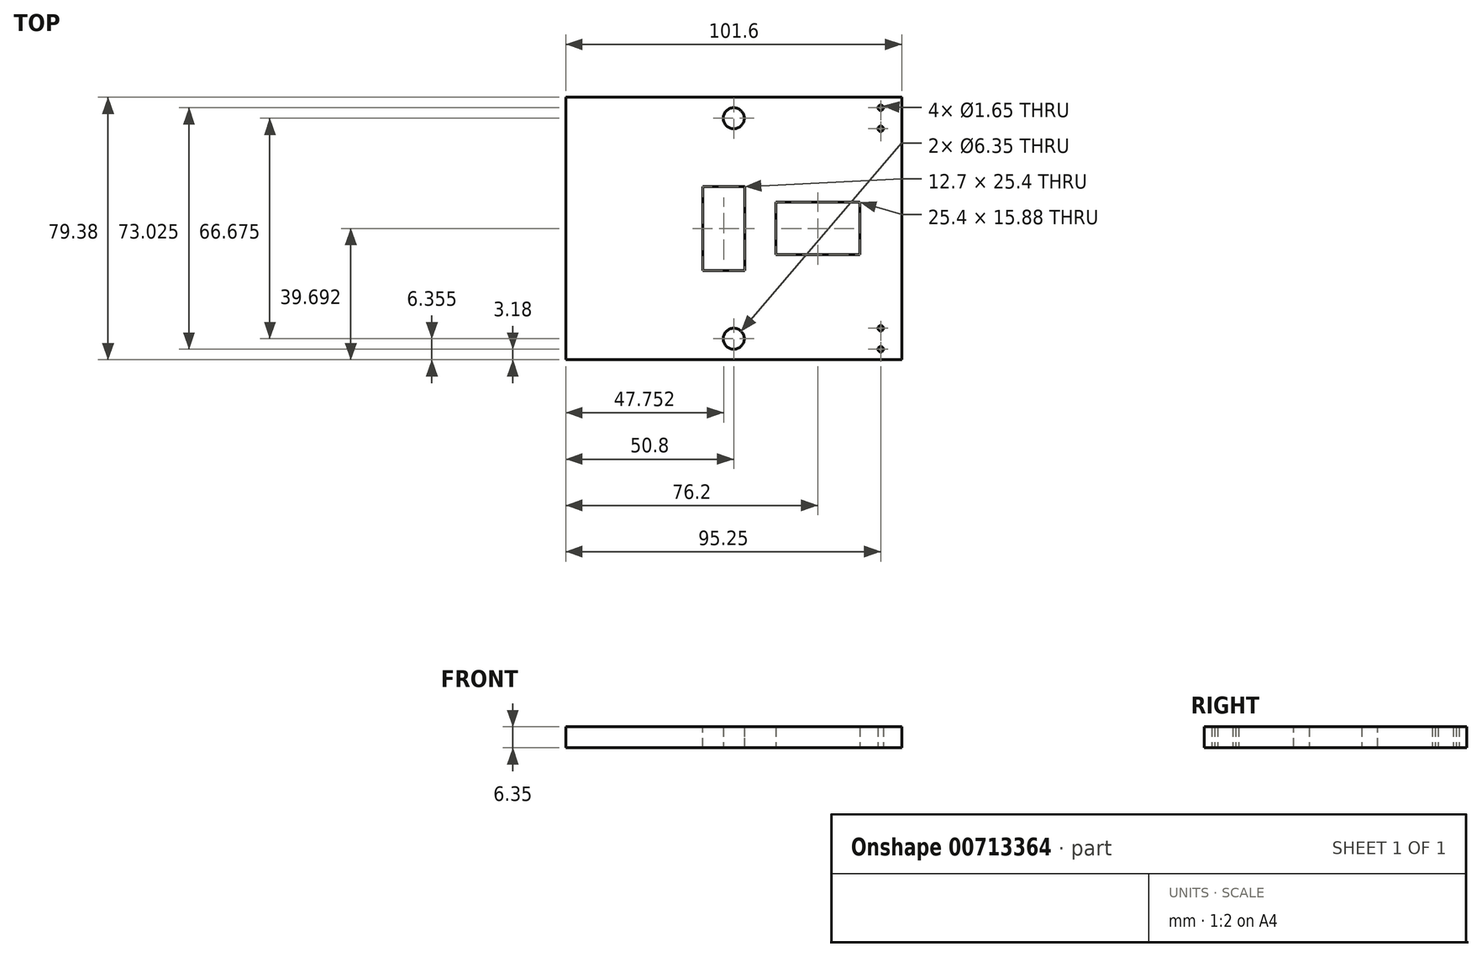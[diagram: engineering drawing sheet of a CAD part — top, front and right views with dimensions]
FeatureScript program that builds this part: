
annotation { "Feature Type Name" : "Feature", "Feature Type Description" : "" }
export const myFeature = defineFeature(function(context is Context, id is Id, definition is map)
    precondition{}
    {
        {
            var Q0;
            Q0=qCreatedBy(makeId("Top.planeOp"),FACE);
            var sketch = newSketch(context, id + "F0", { "sketchPlane" : qUnion([Q0])});
            skLineSegment(sketch, "E0.bottom", {"start": v(0, 0) * mm, "end": v(-101.6, 0) * mm});
            skLineSegment(sketch, "E0.top", {"start": v(0, -79.38) * mm, "end": v(-101.6, -79.38) * mm});
            skLineSegment(sketch, "E0.left", {"start": v(0, 0) * mm, "end": v(0, -79.38) * mm});
            skLineSegment(sketch, "E0.right", {"start": v(-101.6, 0) * mm, "end": v(-101.6, -79.38) * mm});
            skLineSegment(sketch, "E1.bottom", {"start": v(0, 0) * mm, "end": v(-12.7, 0) * mm});
            skLineSegment(sketch, "E1.top", {"start": v(0, -12.7) * mm, "end": v(-12.7, -12.7) * mm});
            skLineSegment(sketch, "E1.left", {"start": v(0, 0) * mm, "end": v(0, -12.7) * mm});
            skLineSegment(sketch, "E1.right", {"start": v(-12.7, 0) * mm, "end": v(-12.7, -12.7) * mm});
            skLineSegment(sketch, "E2.bottom", {"start": v(0, -79.38) * mm, "end": v(-12.7, -79.38) * mm});
            skLineSegment(sketch, "E2.top", {"start": v(0, -66.67) * mm, "end": v(-12.7, -66.67) * mm});
            skLineSegment(sketch, "E2.left", {"start": v(0, -79.38) * mm, "end": v(0, -66.67) * mm});
            skLineSegment(sketch, "E2.right", {"start": v(-12.7, -79.38) * mm, "end": v(-12.7, -66.67) * mm});
            skPoint(sketch, "E3", {"position": v(-6.35, 0) * mm});
            skLineSegment(sketch, "E4", {"start": v(-6.35, 0) * mm, "end": v(-6.35, -12.7) * mm});
            skPoint(sketch, "E5", {"position": v(-6.35, -9.53) * mm});
            skPoint(sketch, "E6", {"position": v(-6.35, -3.18) * mm});
            skCircle(sketch, "E7", {"center": v(-6.35, -3.18) * mm, "radius": 0.83 * mm});
            skCircle(sketch, "E8", {"center": v(-6.35, -9.53) * mm, "radius": 0.83 * mm});
            skPoint(sketch, "E9", {"position": v(-6.35, -66.67) * mm});
            skLineSegment(sketch, "E10", {"start": v(-6.35, -66.67) * mm, "end": v(-6.35, -79.38) * mm});
            skPoint(sketch, "E11", {"position": v(-6.35, -69.85) * mm});
            skPoint(sketch, "E12", {"position": v(-6.35, -76.2) * mm});
            skCircle(sketch, "E13", {"center": v(-6.35, -76.2) * mm, "radius": 0.83 * mm});
            skCircle(sketch, "E14", {"center": v(-6.35, -69.85) * mm, "radius": 0.83 * mm});
            skLineSegment(sketch, "E15", {"start": v(-50.8, 0) * mm, "end": v(-50.8, -6.35) * mm});
            skCircle(sketch, "E16", {"center": v(-50.8, -6.35) * mm, "radius": 3.18 * mm});
            skLineSegment(sketch, "E17", {"start": v(-50.8, -79.38) * mm, "end": v(-50.8, -73.03) * mm});
            skCircle(sketch, "E18", {"center": v(-50.8, -73.03) * mm, "radius": 3.18 * mm});
            skLineSegment(sketch, "E19", {"start": v(0, 0) * mm, "end": v(0, -31.75) * mm});
            skLineSegment(sketch, "E20", {"start": v(0, -31.75) * mm, "end": v(0, -47.62) * mm});
            skLineSegment(sketch, "E21", {"start": v(0, -47.62) * mm, "end": v(0, -79.38) * mm});
            skLineSegment(sketch, "E22", {"start": v(0, -31.75) * mm, "end": v(-52.42, -31.75) * mm});
            skLineSegment(sketch, "E23", {"start": v(0, -47.62) * mm, "end": v(-52.42, -47.62) * mm});
            skLineSegment(sketch, "E24", {"start": v(-38.1, -31.75) * mm, "end": v(-38.1, -47.62) * mm});
            skLineSegment(sketch, "E25", {"start": v(-12.7, -31.75) * mm, "end": v(-12.7, -47.62) * mm});
            skSolve(sketch);
        }
        {
            var Q0;
            Q0 = qSketchRegion(id + "F0", true);
            extrude(context, id + "F1", {"entities" : qUnion([Q0]), "depth" : 6.35 * mm, "offsetDistance" : 25.4 * mm});
        }
        {
            var Q0;
            Q0=makeQuery(id+"F1.opExtrude","CAP_FACE",FACE,{"disambiguationData":[OSD([sQuery(id+"F0.wireOp",EDGE,"E0.bottom"),sQuery(id+"F0.wireOp",EDGE,"E0.top"),sQuery(id+"F0.wireOp",EDGE,"E0.left"),sQuery(id+"F0.wireOp",EDGE,"E0.right"),sQuery(id+"F0.wireOp",EDGE,"E1.bottom"),sQuery(id+"F0.wireOp",EDGE,"E1.left"),sQuery(id+"F0.wireOp",EDGE,"E2.bottom"),sQuery(id+"F0.wireOp",EDGE,"E2.left"),sQuery(id+"F0.wireOp",EDGE,"E7"),sQuery(id+"F0.wireOp",EDGE,"E8"),sQuery(id+"F0.wireOp",EDGE,"E13"),sQuery(id+"F0.wireOp",EDGE,"E14")])],"isStart":false});
            var sketch = newSketch(context, id + "F2", { "sketchPlane" : qUnion([Q0])});
            skLineSegment(sketch, "E26.bottom", {"start": v(0, 0) * mm, "end": v(-53.85, 0) * mm});
            skLineSegment(sketch, "E26.top", {"start": v(0, -39.69) * mm, "end": v(-53.85, -39.69) * mm});
            skLineSegment(sketch, "E26.left", {"start": v(0, 0) * mm, "end": v(0, -39.69) * mm});
            skLineSegment(sketch, "E26.right", {"start": v(-53.85, 0) * mm, "end": v(-53.85, -39.69) * mm});
            skLineSegment(sketch, "E27.bottom", {"start": v(-47.5, -26.99) * mm, "end": v(-60.2, -26.99) * mm});
            skLineSegment(sketch, "E27.top", {"start": v(-47.5, -52.39) * mm, "end": v(-60.2, -52.39) * mm});
            skLineSegment(sketch, "E27.left", {"start": v(-47.5, -26.99) * mm, "end": v(-47.5, -52.39) * mm});
            skLineSegment(sketch, "E27.right", {"start": v(-60.2, -26.99) * mm, "end": v(-60.2, -52.39) * mm});
            skPoint(sketch, "E27.middle", {"position": v(-53.85, -39.69) * mm});
            skSolve(sketch);
        }
        {
            var Q0;
            Q0=makeQuery(id+"F2.imprint","IMPRINT",FACE,{"disambiguationData":[TD([[makeQuery(id+"F2.imprint","IMPRINT",EDGE,{"derivedFrom":makeQuery(id+"F1.opExtrude","CAP_EDGE",EDGE,{"disambiguationData":[OSD([sQuery(id+"F0.wireOp",EDGE,"E7")])],"isStart":false})}),1.0]])]});
            var Q1;
            Q1=makeQuery(id+"F2.imprint","IMPRINT",FACE,{"disambiguationData":[TD([[makeQuery(id+"F2.imprint","IMPRINT",EDGE,{"derivedFrom":makeQuery(id+"F1.opExtrude","CAP_EDGE",EDGE,{"disambiguationData":[OSD([sQuery(id+"F0.wireOp",EDGE,"E8")])],"isStart":false})}),1.0]])]});
            var Q2;
            {var subQ0=sQuery(id+"F2.wireOp",EDGE,"E26.right");var subQ1=sQuery(id+"F2.wireOp",EDGE,"E26.top");var subQ2=makeQuery(id+"F2.imprint","INTERSECT",VERTEX,{"derivedFrom":[subQ1,subQ0]});Q2=makeQuery(id+"F2.imprint","IMPRINT",FACE,{"disambiguationData":[TD([[makeQuery(id+"F2.imprint","IMPRINT",EDGE,{"disambiguationData":[TD([[subQ2,1.0]])],"derivedFrom":subQ1}),-1.0]])]});}
            var Q3;
            {var subQ0=sQuery(id+"F2.wireOp",EDGE,"E27.top");Q3=makeQuery(id+"F2.imprint","IMPRINT",FACE,{"disambiguationData":[TD([[makeQuery(id+"F2.imprint","IMPRINT",EDGE,{"derivedFrom":subQ0}),-1.0]])]});}
            extrude(context, id + "F3", {"entities" : qUnion([Q0, Q1, Q2, Q3]), "operationType" : NewBodyOperationType.REMOVE, "oppositeDirection" : true, "depth" : 25.4 * mm, "offsetDistance" : 25.4 * mm});
        }
    });
